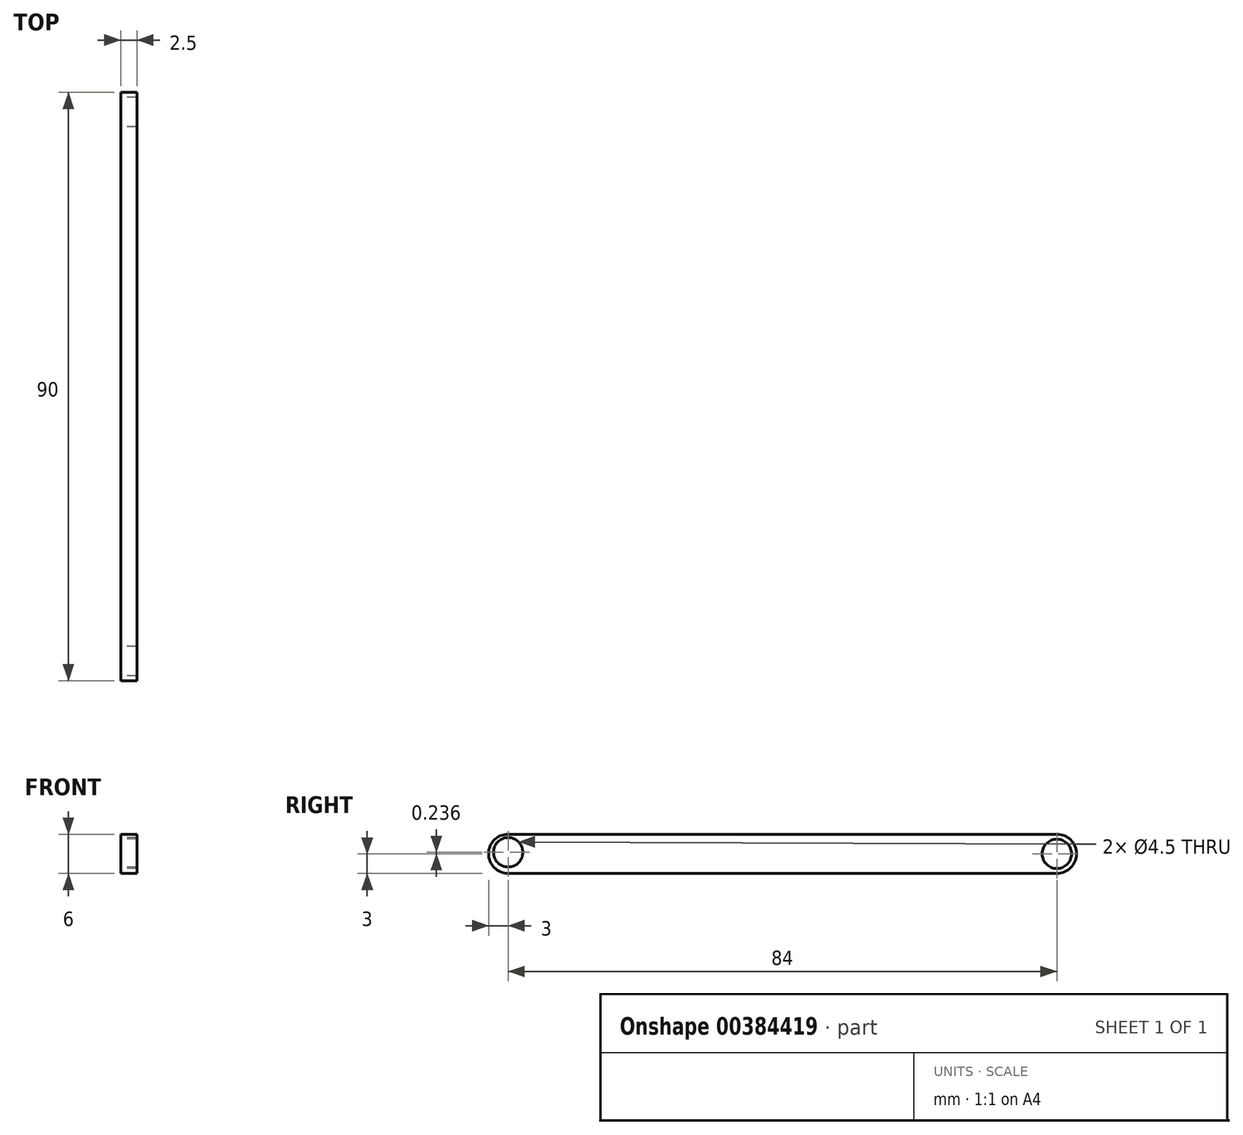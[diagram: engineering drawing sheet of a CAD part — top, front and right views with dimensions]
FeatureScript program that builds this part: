
annotation { "Feature Type Name" : "Feature", "Feature Type Description" : "" }
export const myFeature = defineFeature(function(context is Context, id is Id, definition is map)
    precondition{}
    {
        {
            var Q0;
            Q0=qCreatedBy(makeId("Front.planeOp"),FACE);
            var sketch = newSketch(context, id + "F0", { "sketchPlane" : qUnion([Q0])});
            skLineSegment(sketch, "E0.bottom", {"start": v(1.25, 3) * mm, "end": v(-1.25, 3) * mm});
            skLineSegment(sketch, "E0.top", {"start": v(1.25, -3) * mm, "end": v(-1.25, -3) * mm});
            skLineSegment(sketch, "E0.left", {"start": v(1.25, 3) * mm, "end": v(1.25, -3) * mm});
            skLineSegment(sketch, "E0.right", {"start": v(-1.25, 3) * mm, "end": v(-1.25, -3) * mm});
            skPoint(sketch, "E0.middle", {"position": v(0, 0) * mm});
            skSolve(sketch);
        }
        {
            var Q0;
            Q0 = qSketchRegion(id + "F0", true);
            extrude(context, id + "F1", {"entities" : qUnion([Q0]), "depth" : 90 * mm});
        }
        {
            var Q0;
            Q0=makeQuery(id+"F1.opExtrude","SWEPT_FACE",FACE,{"disambiguationData":[OSD([sQuery(id+"F0.wireOp",EDGE,"E0.right")])]});
            var sketch = newSketch(context, id + "F2", { "sketchPlane" : qUnion([Q0])});
            skCircle(sketch, "E1", {"center": v(3, 0) * mm, "radius": 2.25 * mm});
            skSolve(sketch);
        }
        {
            var Q0;
            Q0=makeQuery(id+"F2.imprint","IMPRINT",FACE,{"disambiguationData":[TD([[makeQuery(id+"F2.imprint","IMPRINT",EDGE,{"derivedFrom":sQuery(id+"F2.wireOp",EDGE,"E1")}),1.0]])]});
            extrude(context, id + "F3", {"entities" : qUnion([Q0]), "operationType" : NewBodyOperationType.REMOVE, "oppositeDirection" : true, "depth" : 25 * mm});
        }
        {
            var Q0;
            Q0=makeQuery(id+"F1.opExtrude","CAP_EDGE",EDGE,{"disambiguationData":[OSD([sQuery(id+"F0.wireOp",EDGE,"E0.bottom")])],"isStart":true});
            var Q1;
            Q1=makeQuery(id+"F1.opExtrude","CAP_EDGE",EDGE,{"disambiguationData":[OSD([sQuery(id+"F0.wireOp",EDGE,"E0.top")])],"isStart":true});
            fillet(context, id + "F4", {"entities" : qUnion([Q0, Q1]), "radius" : 3 * mm, "tangentPropagation" : true, "allowEdgeOverflow" : false});
        }
        {
            var Q0;
            Q0=makeQuery(id+"F1.opExtrude","SWEPT_FACE",FACE,{"disambiguationData":[OSD([sQuery(id+"F0.wireOp",EDGE,"E0.right")])]});
            var sketch = newSketch(context, id + "F5", { "sketchPlane" : qUnion([Q0])});
            skCircle(sketch, "E2", {"center": v(87, 0.24) * mm, "radius": 2.25 * mm});
            skSolve(sketch);
        }
        {
            var Q0;
            Q0=makeQuery(id+"F5.imprint","IMPRINT",FACE,{"disambiguationData":[TD([[makeQuery(id+"F5.imprint","IMPRINT",EDGE,{"derivedFrom":sQuery(id+"F5.wireOp",EDGE,"E2")}),1.0]])]});
            extrude(context, id + "F6", {"entities" : qUnion([Q0]), "operationType" : NewBodyOperationType.REMOVE, "oppositeDirection" : true, "depth" : 25 * mm});
        }
        {
            var Q0;
            Q0=makeQuery(id+"F1.opExtrude","CAP_EDGE",EDGE,{"disambiguationData":[OSD([sQuery(id+"F0.wireOp",EDGE,"E0.bottom")])],"isStart":false});
            var Q1;
            Q1=makeQuery(id+"F1.opExtrude","CAP_EDGE",EDGE,{"disambiguationData":[OSD([sQuery(id+"F0.wireOp",EDGE,"E0.top")])],"isStart":false});
            fillet(context, id + "F7", {"entities" : qUnion([Q0, Q1]), "radius" : 3 * mm, "tangentPropagation" : true, "allowEdgeOverflow" : false});
        }
    });
